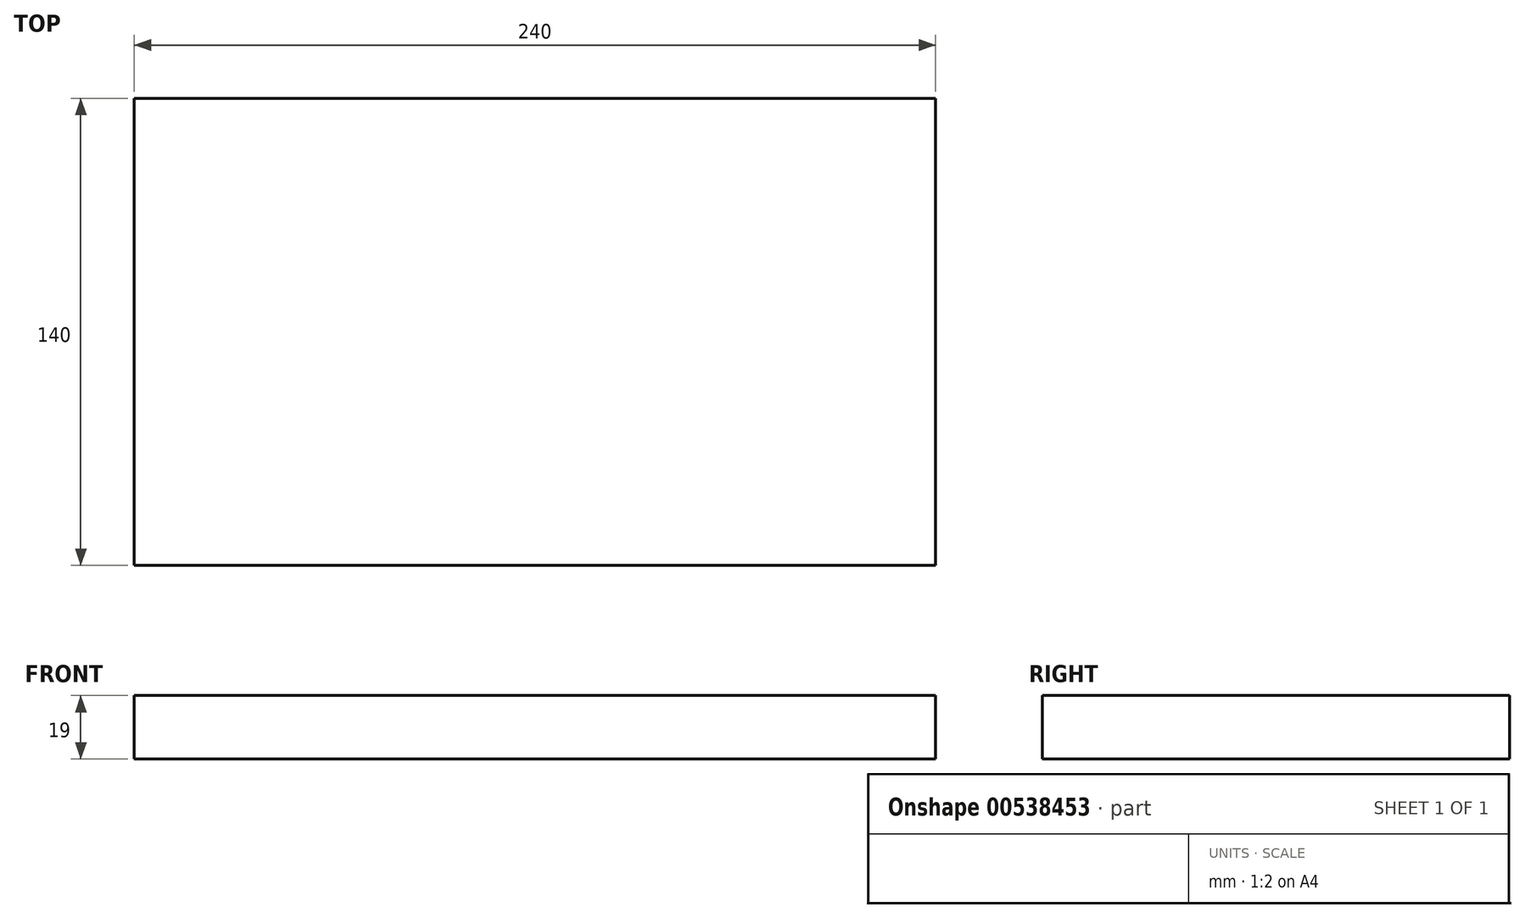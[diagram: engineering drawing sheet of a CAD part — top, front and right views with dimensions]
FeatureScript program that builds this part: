
annotation { "Feature Type Name" : "Feature", "Feature Type Description" : "" }
export const myFeature = defineFeature(function(context is Context, id is Id, definition is map)
    precondition{}
    {
        {
            var Q0;
            Q0=qCreatedBy(makeId("Top.planeOp"),FACE);
            var sketch = newSketch(context, id + "F0", { "sketchPlane" : qUnion([Q0])});
            skLineSegment(sketch, "E0.bottom", {"start": v(120, 70) * mm, "end": v(-120, 70) * mm});
            skLineSegment(sketch, "E0.top", {"start": v(120, -70) * mm, "end": v(-120, -70) * mm});
            skLineSegment(sketch, "E0.left", {"start": v(120, 70) * mm, "end": v(120, -70) * mm});
            skLineSegment(sketch, "E0.right", {"start": v(-120, 70) * mm, "end": v(-120, -70) * mm});
            skPoint(sketch, "E0.middle", {"position": v(0, 0) * mm});
            skSolve(sketch);
        }
        {
            var Q0;
            Q0 = qSketchRegion(id + "F0", true);
            extrude(context, id + "F1", {"entities" : qUnion([Q0]), "depth" : 19 * mm, "offsetDistance" : 25 * mm});
        }
    });
